# Revit family: ledtallinn-p_l15-45w-ble2-tw-d_i-u10-bl_529000106100_2da1
name_source: partatom
category: Lighting Fixtures
units: mm (PartAtom-declared; Revit-internal decimal feet)

## family parameters
Cut with Voids When Loaded = No
Host = Face
Light Source = No
Part Type = Normal
Room Calculation Point = No
Round Connector Dimension = Use Diameter
Shared = No

## types (1)
- LEDTallinn-P L15-45W-BLE2-TW-D/I-U10-BL (1 x LED, 4050 lm, 4000)
    Apparent Load = 45 VA
    Approval mark = CE, ENEC
    CIE Flux Codes = 98 100 100 46 207
    Color Rendering = 90
    Color Temperature = 4000
    Control Gear = Electronic ballast
    Default Elevation = 1800 mm
    Description = Suspended Linear Tallinn 1500mm-45W-4050lm-2700/6500K-120°x50°-Black-UGR10
    Frequency = 60 Hz
    Height = 100 mm  [stored 0.328084 ft]
    Lamp = 1 x LED
    Lamp Light Flux = 4050 lm
    Lamp count = 1
    Length = 1500 mm
    Luminous efficacy = 187 lm/W
    Manufacturer = OPPLE
    ModVariant = No
    Model = 529000106100
    Mounting Place = Ceiling
    Mounting Type = Surface mounted
    Number of Poles = 1
    OnlyDefault = Yes
    Power Factor = 1
    Product Name = LEDTallinn-P L15-45W-BLE2-TW-D/I-U10-BL
    Product group = Ceiling mounted luminaire
    ProductGroupID = 3
    Protection Class = Protection class I
    Protection Degree = IP 20
    RLX_Detail_Level = 1
    RLX_Emergency_Light_Flux = 0 lm
    RLX_Emergency_Type = 0
    RLX_Emergency_Type_DB = No
    RlxData = <blob elided: 375513 chars, md5=1ecc8886>
    Socket = socket
    Standby Power = 0 W
    System Light Flux = 8398 lm
    System Power = 45 W
    Type Comments = Product without accessories
    Type Image = web_tallinn_grille_l15_bl.jpg
    URL = http://relux.com
    VarID = ---
    Voltage = 230 V
    Voltage Range = 220-240 V
    Weight = 0.00 kg
    Width = 35 mm

note: [stored X ft] marks values corroborated as IEEE doubles in the binary element streams (Revit-internal decimal feet)

## geometry (parser evidence)
native form markers: Blend x4, Sweep x10
no freeform markers — native parametric forms only
